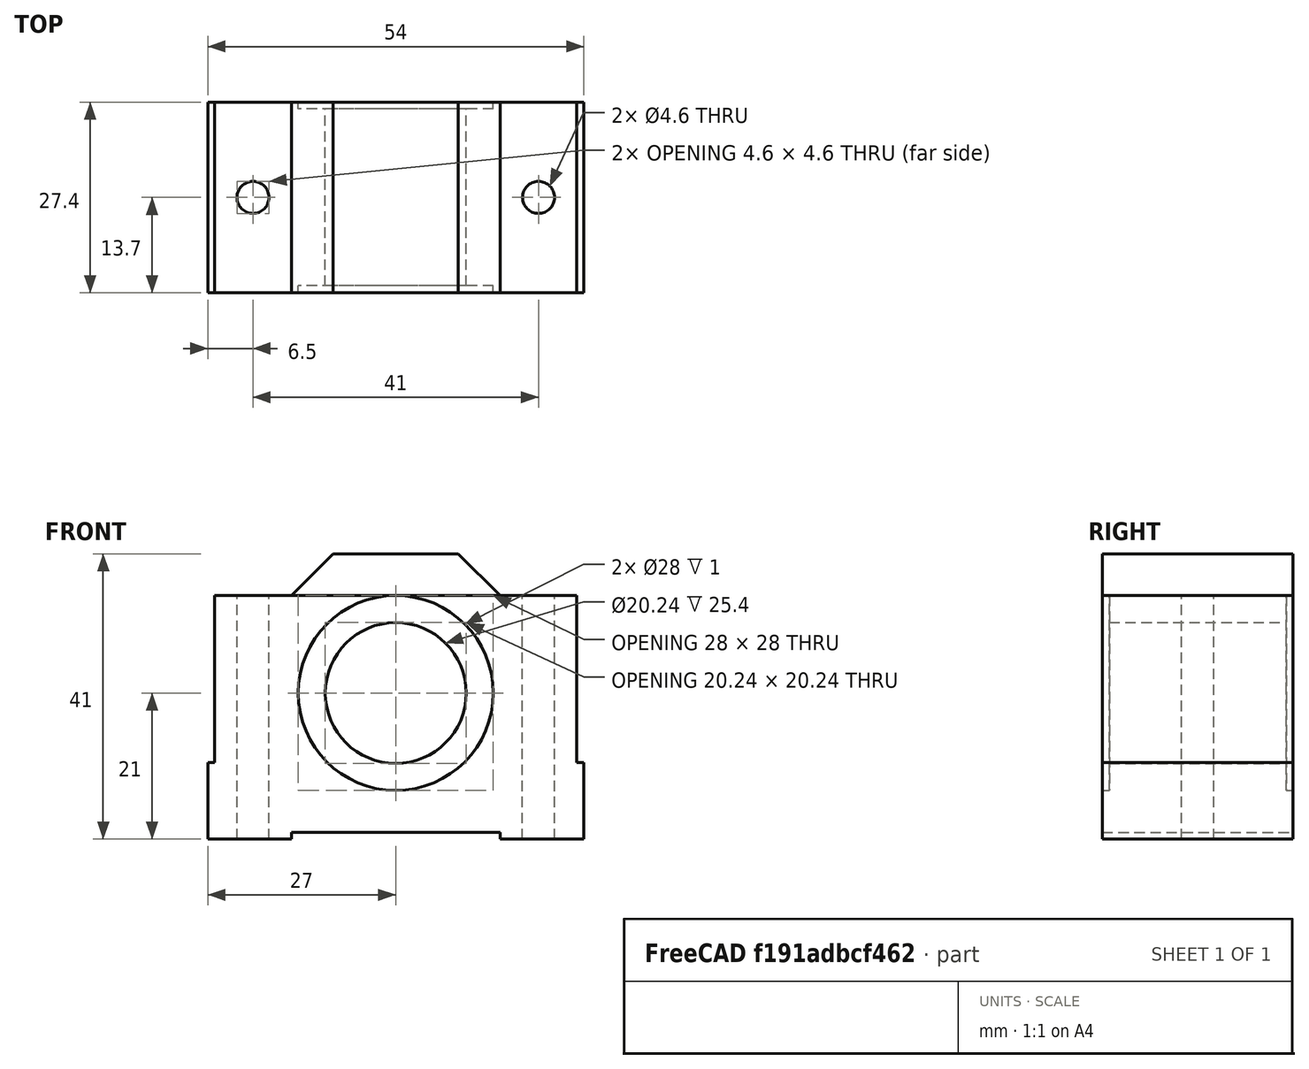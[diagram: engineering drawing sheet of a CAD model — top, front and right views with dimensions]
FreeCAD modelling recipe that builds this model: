
FCSTD DOCUMENT
Label: SC20VUU
objects: Part::Cut×10, Part::Box×7, Part::Cylinder×5, Part::MultiFuse×1
note: 23 computed .brp shape members not serialized (recipe doc carries the construction recipe); baked Part::Feature solids carry a one-line shape summary decoded from their .brp

FEATURE [Part::Box] Box
  Height = 35
  Length = 54
  Width = 27.4
FEATURE [Part::Cylinder] Cylinder
  Angle = 360
  Height = 60
  Placement = pos=(27,-19.76,21) rot=(-1,0,0;1.5708rad)
  Radius = 10.12
FEATURE [Part::Cut] Cut
  Base = -> Box
  Placement = pos=(0,-0.000294295,0) rot=(0,0,1;0rad)
  Tool = -> Cylinder
FEATURE [Part::Box] Box001
  Height = 6
  Length = 30
  Width = 27.4
FEATURE [Part::Box] Box002
  Height = 40
  Length = 10
  Placement = pos=(0,-4,0) rot=(0,-1,0;0.785397rad)
  Width = 40
FEATURE [Part::Cut] Cut001
  Base = -> Box001
  Tool = -> Box002
FEATURE [Part::Box] Box003
  Height = 40
  Length = 10
  Placement = pos=(30,-5,0) rot=(0,-1,0;0.785398rad)
  Width = 40
FEATURE [Part::Cut] Cut002
  Base = -> Cut001
  Placement = pos=(12,-0.000271388,35) rot=(0,0,1;0rad)
  Tool = -> Box003
FEATURE [Part::MultiFuse] Fusion
  Shapes = -> [Cut,Cut002]
FEATURE [Part::Box] Box004
  Height = 40
  Length = 10
  Placement = pos=(-9,-7,11) rot=(0,0,1;0rad)
  Width = 50
FEATURE [Part::Cut] Cut003
  Base = -> Fusion
  Tool = -> Box004
FEATURE [Part::Box] Box005
  Height = 40
  Length = 10
  Placement = pos=(53,-9,11) rot=(0,0,1;0rad)
  Width = 50
FEATURE [Part::Cut] Cut004
  Base = -> Cut003
  Tool = -> Box005
FEATURE [Part::Box] Box006
  Height = 10
  Length = 30
  Placement = pos=(12,-12,-9) rot=(0,0,1;0rad)
  Width = 50
FEATURE [Part::Cut] Cut005
  Base = -> Cut004
  Tool = -> Box006
FEATURE [Part::Cylinder] Cylinder001
  Angle = 360
  Height = 10
  Placement = pos=(27,-9,21) rot=(-1,0,0;1.5708rad)
  Radius = 14
FEATURE [Part::Cylinder] Cylinder002
  Angle = 360
  Height = 10
  Placement = pos=(27,26.4,21) rot=(-1,0,0;1.5708rad)
  Radius = 14
FEATURE [Part::Cut] Cut006
  Base = -> Cut005
  Tool = -> Cylinder001
FEATURE [Part::Cut] Cut007
  Base = -> Cut006
  Tool = -> Cylinder002
FEATURE [Part::Cylinder] Cylinder003
  Angle = 360
  Height = 40
  Placement = pos=(6.5,13.7,-2) rot=(0,0,1;0rad)
  Radius = 2.3
FEATURE [Part::Cut] Cut008
  Base = -> Cut007
  Tool = -> Cylinder003
FEATURE [Part::Cylinder] Cylinder004
  Angle = 360
  Height = 50
  Placement = pos=(47.5,13.7,-6) rot=(0,0,1;0rad)
  Radius = 2.3
FEATURE [Part::Cut] Cut009
  Base = -> Cut008
  Tool = -> Cylinder004
